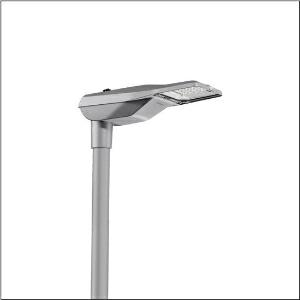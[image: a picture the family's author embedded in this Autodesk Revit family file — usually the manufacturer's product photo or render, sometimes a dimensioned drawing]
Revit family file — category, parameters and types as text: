
# Revit family: streetlight_sl_21_micro___st0_8a_5xe1c43s08db_42f9
name_source: partatom
category: Lighting Fixtures
units: mm (PartAtom-declared; Revit-internal decimal feet)

## family parameters
Cut with Voids When Loaded = No
Host = Face
Light Source = No
Part Type = Normal
Room Calculation Point = No
Round Connector Dimension = Use Diameter
Shared = No

## types (1)
- --- (1 x LED, 5320 lm, 39.1 W, 4000K)
    Apparent Load = 39 VA
    CIE Flux Codes = 38 75 97 100 100
    Color Rendering = 70
    Color Temperature = 4000K
    Default Elevation = 1800 mm
    Description = Streetlight SL 21 micro, mast luminaire, primary light control with lens, of PMMA, primary optical cover: cover, of toughened safety glass, transparent, light distribution: ST0.8a, light emission: direct distribution, primary light characteristic: asymmetric, installation type: side-entry, post-top, LED, High Power LED, rated luminous flux: 5.320lm, luminous efficacy: 136lm/W, light colour: 740, colour temperature: 4000K, control: flexible luminous flux parameterisation, time-dependent luminous flux control, constant luminous flux control, overheat protection, presetting dimming logarithmic, mains connection: 220..240V, AC, 50/60Hz, start of lifetime: 39W, end of service life: 41W, reduction: 18W, luminaire housing, of diecast aluminium, powder-coated, Siteco® metallic grey (DB 702S), corrosivity category C5 mid according to DIN EN ISO 12944, please order mast flange separately, inclination adjustable: 0°, 5°, 10°, 15°, sealing non-destructively replaceable, multi-level sealing system, length: 528mm, width: 235mm, height: 110mm, mast flange for spigot size: 42mm (side-entry): 5XC10008XM4, 60/48mm (side-entry/post-top): 5XC10108XM2, 76/60mm (side-entry/post-top): 5XC10108XM1, Smart Interface above, protection rating (complete): IP66, insulation class (complete): insulation class II (safety insulation), certification: CE, ENEC, ENEC+, VDE, impact resistance: IK09, permissible operating ambient temperature for outdoor applications: -40..+50°C, standard-compliant lighting for roads and squares, packaging unit: 1 piece

Light Distribution: ST0.8a
    Height = 110 mm
    Lamp = 1 x LED
    Lamp Light Flux = 5320 lm
    Lamp Power = 39.1 W
    Lamp count = 1
    Length = 528 mm
    Luminous efficacy = 136 lm/W
    Manufacturer = Siteco
    ModVariant = No
    Model = 5XE1C43S08DB
    Number of Poles = 1
    OnlyDefault = Yes
    Power Factor = 1
    Product Name = Streetlight SL 21 micro | ST0.8a
    Product group = mast luminaire | pylon top
    ProductGroupID = 6100
    Protection Class = Protection class II
    Protection Degree = IP 66
    RLX_Detail_Level = 1
    RLX_Emergency_Light_Flux = 0 lm
    RLX_Emergency_Type = 0
    RLX_Emergency_Type_DB = No
    RlxData = <blob elided: 98445 chars, md5=a7803f88>
    Socket = socket
    Standby Power = 0 W
    System Light Flux = 5320 lm
    System Power = 39 W
    Type Comments = factory setting: luminous flux: 100 % | dim-lin: 254 | 765 mA
    Type Image = l_1277292.jpg
    URL = http://relux.com
    VarID = @adj_104545
    Voltage = 0 V
    Weight = 0.00 kg
    Width = 235 mm

## geometry (parser evidence)
native form markers: Blend x4, Sweep x10
no freeform markers — native parametric forms only
